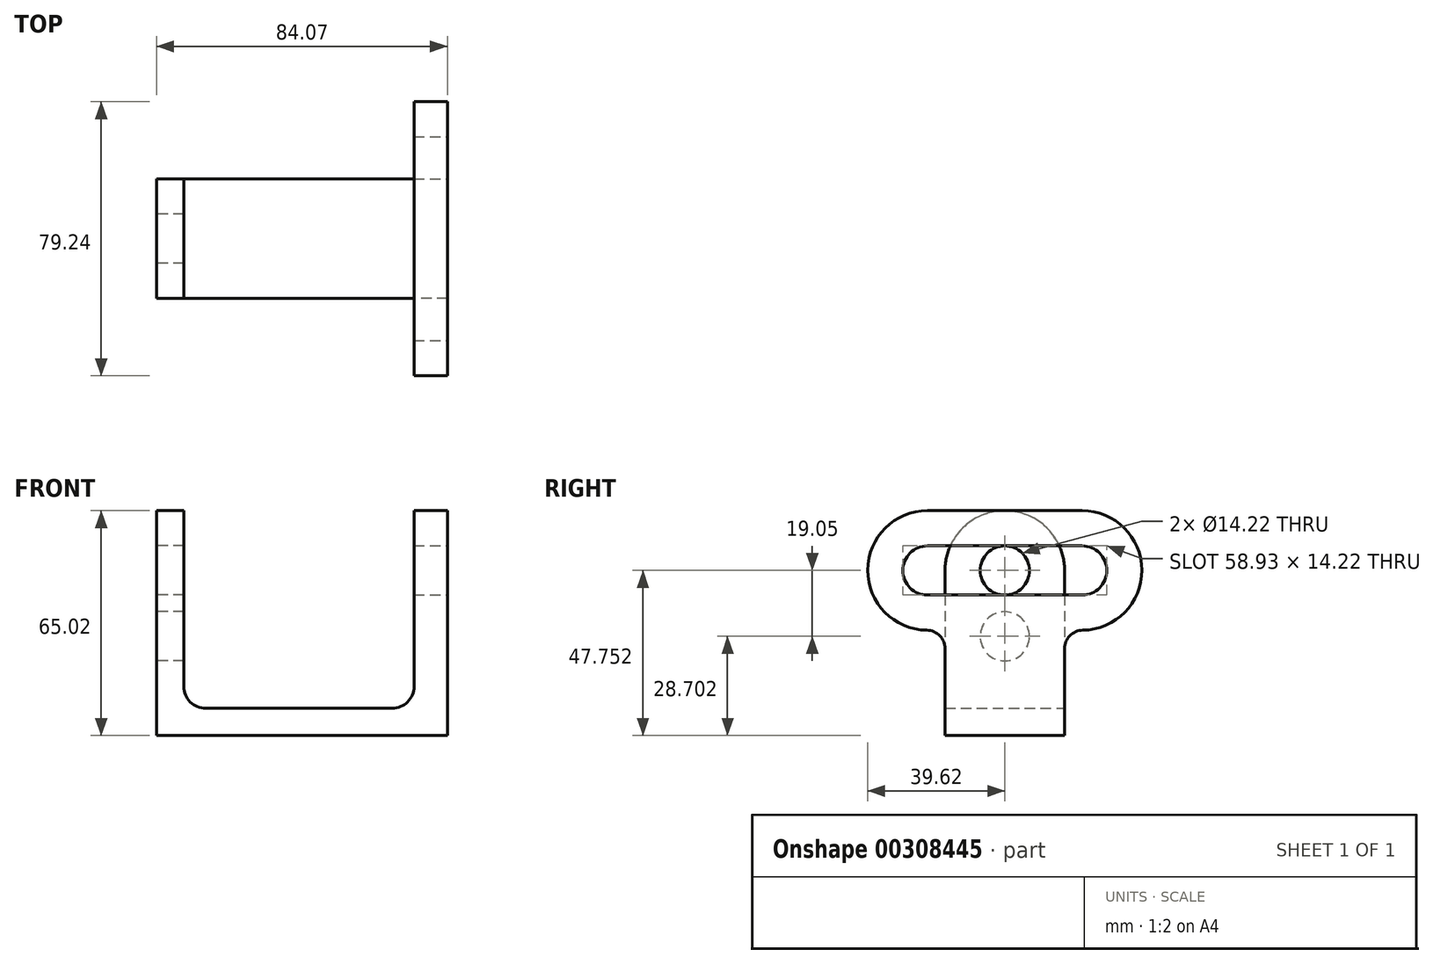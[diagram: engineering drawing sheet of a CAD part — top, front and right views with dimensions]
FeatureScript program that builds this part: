
annotation { "Feature Type Name" : "Feature", "Feature Type Description" : "" }
export const myFeature = defineFeature(function(context is Context, id is Id, definition is map)
    precondition{}
    {
        {
            var Q0;
            Q0=qCreatedBy(makeId("Front.planeOp"),FACE);
            var sketch = newSketch(context, id + "F0", { "sketchPlane" : qUnion([Q0])});
            skLineSegment(sketch, "E0.bottom", {"start": v(0, 0) * mm, "end": v(84.07, 0) * mm});
            skLineSegment(sketch, "E0.top", {"start": v(0, 47.75) * mm, "end": v(7.87, 47.75) * mm});
            skLineSegment(sketch, "E0.left", {"start": v(0, 0) * mm, "end": v(0, 47.75) * mm});
            skLineSegment(sketch, "E0.right", {"start": v(84.07, 0) * mm, "end": v(84.07, 47.75) * mm});
            skLineSegment(sketch, "E1.top", {"start": v(7.87, 7.87) * mm, "end": v(74.42, 7.87) * mm});
            skLineSegment(sketch, "E1.left", {"start": v(7.87, 47.75) * mm, "end": v(7.87, 7.87) * mm});
            skLineSegment(sketch, "E1.right", {"start": v(74.42, 47.75) * mm, "end": v(74.42, 7.87) * mm});
            skLineSegment(sketch, "E2.trimOffspring", {"start": v(74.42, 47.75) * mm, "end": v(84.07, 47.75) * mm});
            skSolve(sketch);
        }
        {
            var Q0;
            Q0 = qSketchRegion(id + "F0", true);
            extrude(context, id + "F1", {"entities" : qUnion([Q0]), "endBound" : BoundingType.SYMMETRIC, "depth" : 34.54 * mm});
        }
        {
            var Q0;
            Q0=qCreatedBy(makeId("Right.planeOp"),FACE);
            var sketch = newSketch(context, id + "F2", { "sketchPlane" : qUnion([Q0])});
            skArc(sketch, "E3", {"start": v(17.27, 47.75) * mm, "mid": v(0, 65.02) * mm, "end": v(-17.27, 47.75) * mm});
            skLineSegment(sketch, "E4", {"start": v(17.27, 47.75) * mm, "end": v(-17.27, 47.75) * mm});
            skSolve(sketch);
        }
        {
            var Q0;
            Q0 = qSketchRegion(id + "F2", true);
            extrude(context, id + "F3", {"entities" : qUnion([Q0]), "operationType" : NewBodyOperationType.ADD, "depth" : 7.87 * mm});
        }
        {
            var Q0;
            Q0=makeQuery(id+"F1.opExtrude","SWEPT_FACE",FACE,{"disambiguationData":[OSD([sQuery(id+"F0.wireOp",EDGE,"E0.right")])]});
            var sketch = newSketch(context, id + "F4", { "sketchPlane" : qUnion([Q0])});
            skLineSegment(sketch, "E5", {"start": v(-22.35, 47.75) * mm, "end": v(22.35, 47.75) * mm, "construction": true});
            skLineSegment(sketch, "E6", {"start": v(0, 0) * mm, "end": v(0, 54.86) * mm, "construction": true});
            skArc(sketch, "E7.0.startCap", {"start": v(-22.35, 40.64) * mm, "mid": v(-29.46, 47.75) * mm, "end": v(-22.35, 54.86) * mm});
            skArc(sketch, "E7.0.endCap", {"start": v(22.35, 54.86) * mm, "mid": v(29.46, 47.75) * mm, "end": v(22.35, 40.64) * mm});
            skLineSegment(sketch, "E7.0.left", {"start": v(-22.35, 54.86) * mm, "end": v(22.35, 54.86) * mm});
            skLineSegment(sketch, "E7.0.right", {"start": v(-22.35, 40.64) * mm, "end": v(22.35, 40.64) * mm});
            skLineSegment(sketch, "E8.0", {"start": v(-22.35, 65.02) * mm, "end": v(22.35, 65.02) * mm});
            skArc(sketch, "E8.1", {"start": v(-22.35, 30.48) * mm, "mid": v(-39.62, 47.75) * mm, "end": v(-22.35, 65.02) * mm});
            skLineSegment(sketch, "E8.2", {"start": v(-22.35, 30.48) * mm, "end": v(22.35, 30.48) * mm});
            skArc(sketch, "E8.3", {"start": v(22.35, 65.02) * mm, "mid": v(39.62, 47.75) * mm, "end": v(22.35, 30.48) * mm});
            skSolve(sketch);
        }
        {
            var Q0;
            Q0 = qSketchRegion(id + "F4", true);
            extrude(context, id + "F5", {"entities" : qUnion([Q0]), "operationType" : NewBodyOperationType.ADD, "oppositeDirection" : true, "depth" : 9.65 * mm});
        }
        {
            var Q0;
            {var subQ0=sQuery(id+"F0.wireOp",EDGE,"E2.trimOffspring");var subQ4=sQuery(id+"F0.wireOp",EDGE,"E0.right");Q0=makeQuery(id+"F5.boolean.opBoolean","SPLIT",FACE,{"disambiguationData":[TD([makeQuery(id+"F1.opExtrude","SWEPT_FACE",FACE,{"disambiguationData":[OSD([subQ0])]})])],"derivedFrom":makeQuery(id+"F1.opExtrude","SWEPT_FACE",FACE,{"disambiguationData":[OSD([subQ4])]})});}
            var sketch = newSketch(context, id + "F6", { "sketchPlane" : qUnion([Q0])});
            skLineSegment(sketch, "E9.bottom", {"start": v(-17.27, 40.64) * mm, "end": v(17.27, 40.64) * mm});
            skLineSegment(sketch, "E9.top", {"start": v(-17.27, 47.75) * mm, "end": v(17.27, 47.75) * mm});
            skLineSegment(sketch, "E9.left", {"start": v(-17.27, 40.64) * mm, "end": v(-17.27, 47.75) * mm});
            skLineSegment(sketch, "E9.right", {"start": v(17.27, 40.64) * mm, "end": v(17.27, 47.75) * mm});
            skSolve(sketch);
        }
        {
            var Q0;
            Q0 = qSketchRegion(id + "F6", true);
            extrude(context, id + "F7", {"entities" : qUnion([Q0]), "operationType" : NewBodyOperationType.REMOVE, "oppositeDirection" : true, "depth" : 9.65 * mm});
        }
        {
            var Q0;
            Q0=makeQuery(id+"F3.boolean.opBoolean","MERGE",FACE,{"derivedFrom":[makeQuery(id+"F1.opExtrude","SWEPT_FACE",FACE,{"disambiguationData":[OSD([sQuery(id+"F0.wireOp",EDGE,"E0.left")])]}),makeQuery(id+"F3.opExtrude","CAP_FACE",FACE,{"disambiguationData":[OSD([sQuery(id+"F2.wireOp",EDGE,"E3"),sQuery(id+"F2.wireOp",EDGE,"E4")])],"isStart":true})]});
            var sketch = newSketch(context, id + "F8", { "sketchPlane" : qUnion([Q0])});
            skCircle(sketch, "E10", {"center": v(0, 47.75) * mm, "radius": 7.11 * mm});
            skCircle(sketch, "E11", {"center": v(0, 28.7) * mm, "radius": 7.11 * mm});
            skSolve(sketch);
        }
        {
            var Q0;
            Q0 = qSketchRegion(id + "F8", true);
            extrude(context, id + "F9", {"entities" : qUnion([Q0]), "operationType" : NewBodyOperationType.REMOVE, "oppositeDirection" : true, "depth" : 7.87 * mm});
        }
        {
            var Q0;
            Q0=makeQuery(id+"F1.opExtrude","SWEPT_EDGE",EDGE,{"disambiguationData":[OSD([sQuery(id+"F0.wireOp",EDGE,"E1.top"),sQuery(id+"F0.wireOp",EDGE,"E1.left")])]});
            fillet(context, id + "F10", {"entities" : qUnion([Q0]), "radius" : 6.35 * mm, "tangentPropagation" : true, "allowEdgeOverflow" : false});
        }
        {
            var Q0;
            Q0=makeQuery(id+"F1.opExtrude","SWEPT_EDGE",EDGE,{"disambiguationData":[OSD([sQuery(id+"F0.wireOp",EDGE,"E1.top"),sQuery(id+"F0.wireOp",EDGE,"E1.right")])]});
            fillet(context, id + "F11", {"entities" : qUnion([Q0]), "radius" : 6.35 * mm, "tangentPropagation" : true, "allowEdgeOverflow" : false});
        }
        {
            var Q0;
            Q0=makeQuery(id+"F5.boolean.opBoolean","INTERSECT",EDGE,{"derivedFrom":[makeQuery(id+"F1.opExtrude","CAP_FACE",FACE,{"disambiguationData":[OSD([sQuery(id+"F0.wireOp",EDGE,"E0.bottom"),sQuery(id+"F0.wireOp",EDGE,"E0.top"),sQuery(id+"F0.wireOp",EDGE,"E0.left"),sQuery(id+"F0.wireOp",EDGE,"E0.right"),sQuery(id+"F0.wireOp",EDGE,"E1.top"),sQuery(id+"F0.wireOp",EDGE,"E1.left"),sQuery(id+"F0.wireOp",EDGE,"E1.right"),sQuery(id+"F0.wireOp",EDGE,"E2.trimOffspring")])],"isStart":false}),makeQuery(id+"F5.opExtrude","SWEPT_FACE",FACE,{"disambiguationData":[OSD([sQuery(id+"F4.wireOp",EDGE,"E8.2")])]})]});
            fillet(context, id + "F12", {"entities" : qUnion([Q0]), "radius" : 5.33 * mm, "tangentPropagation" : true, "allowEdgeOverflow" : false});
        }
        {
            var Q0;
            Q0=makeQuery(id+"F5.boolean.opBoolean","INTERSECT",EDGE,{"derivedFrom":[makeQuery(id+"F1.opExtrude","CAP_FACE",FACE,{"disambiguationData":[OSD([sQuery(id+"F0.wireOp",EDGE,"E0.bottom"),sQuery(id+"F0.wireOp",EDGE,"E0.top"),sQuery(id+"F0.wireOp",EDGE,"E0.left"),sQuery(id+"F0.wireOp",EDGE,"E0.right"),sQuery(id+"F0.wireOp",EDGE,"E1.top"),sQuery(id+"F0.wireOp",EDGE,"E1.left"),sQuery(id+"F0.wireOp",EDGE,"E1.right"),sQuery(id+"F0.wireOp",EDGE,"E2.trimOffspring")])],"isStart":true}),makeQuery(id+"F5.opExtrude","SWEPT_FACE",FACE,{"disambiguationData":[OSD([sQuery(id+"F4.wireOp",EDGE,"E8.2")])]})]});
            fillet(context, id + "F13", {"entities" : qUnion([Q0]), "radius" : 5.33 * mm, "tangentPropagation" : true, "allowEdgeOverflow" : false});
        }
    });
